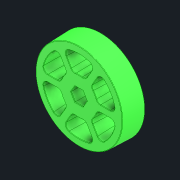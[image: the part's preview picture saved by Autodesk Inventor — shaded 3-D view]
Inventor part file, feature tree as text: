
AUTODESK INVENTOR PART (.ipt)
format: ipt  version: 2021 (Build 250183000, 183)  size: 628,224 bytes
history: native  units: in
note: dims shown in document units (in); Inventor stores cm internally (conversion verified against a paired STEP export)
features: fillet x1
ambient origin geometry x8: Origin, YZ Plane, XZ Plane, XY Plane, X Axis, Y Axis, Z Axis, Center Point
bodies: Solid1 (feature_tree)
feature tree (1):
  fillet  "Fillet3"  [1 undecoded]
note: 1 required parameter value undecoded (feature->parameter linkage not recoverable at this tier; creation-order binding heuristic only, values carry confidence <= 0.55)
